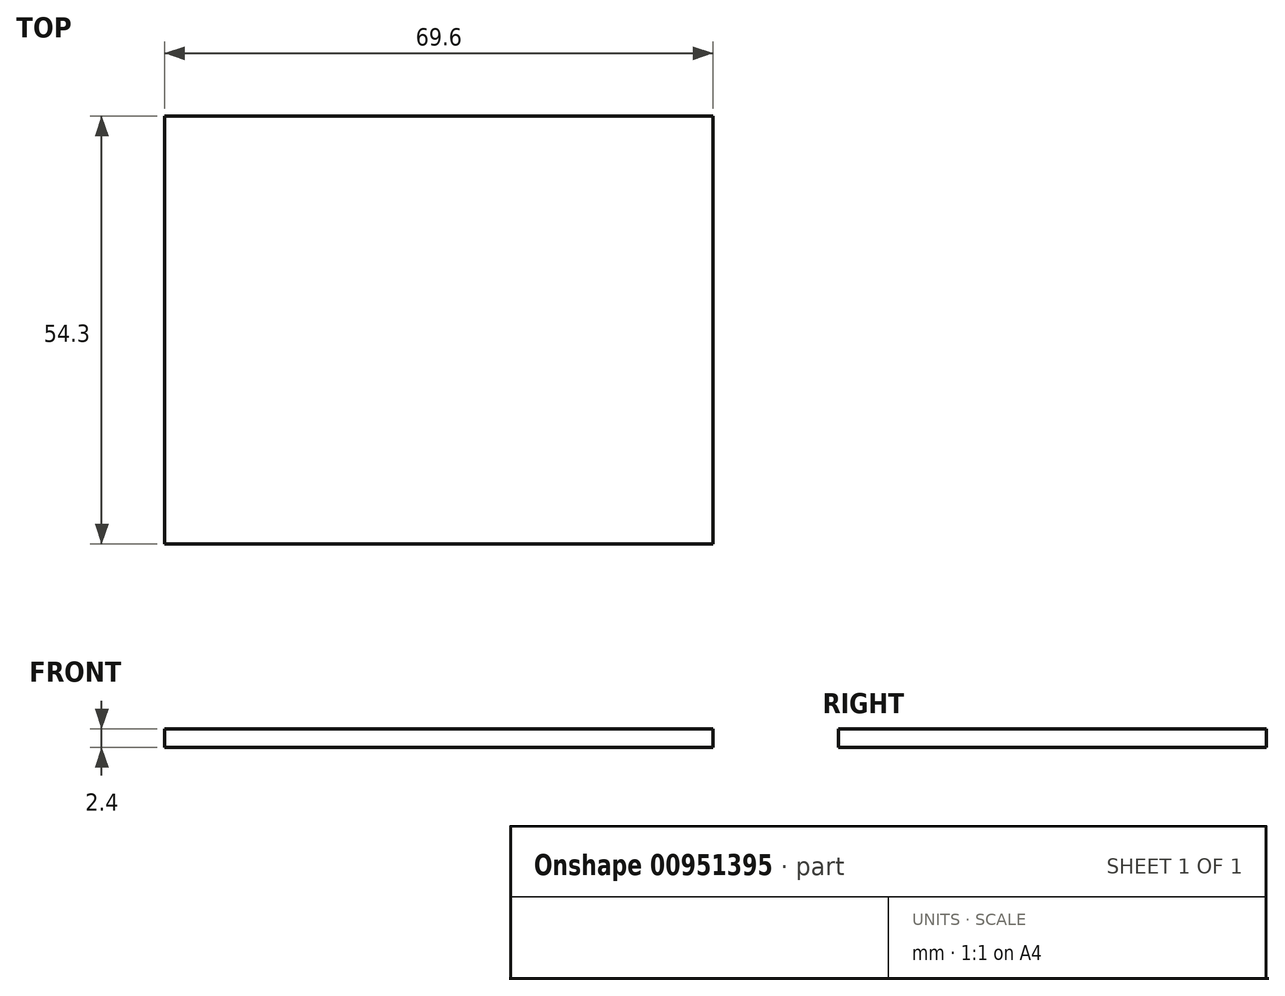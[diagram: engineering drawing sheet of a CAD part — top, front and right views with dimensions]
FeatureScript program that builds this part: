
annotation { "Feature Type Name" : "Feature", "Feature Type Description" : "" }
export const myFeature = defineFeature(function(context is Context, id is Id, definition is map)
    precondition{}
    {
        {
            var Q0;
            Q0=qCreatedBy(makeId("Top.planeOp"),FACE);
            var sketch = newSketch(context, id + "F0", { "sketchPlane" : qUnion([Q0])});
            skLineSegment(sketch, "E0", {"start": v(-69.6, 54.3) * mm, "end": v(-69.6, 0) * mm});
            skLineSegment(sketch, "E1", {"start": v(-69.6, 0) * mm, "end": v(0, 0) * mm});
            skLineSegment(sketch, "E2", {"start": v(0, 0) * mm, "end": v(0, 54.3) * mm});
            skLineSegment(sketch, "E3", {"start": v(0, 54.3) * mm, "end": v(-69.6, 54.3) * mm});
            skSolve(sketch);
        }
        {
            var Q0;
            Q0 = qSketchRegion(id + "F0", true);
            extrude(context, id + "F1", {"entities" : qUnion([Q0]), "depth" : 2.4 * mm, "offsetDistance" : 25 * mm});
        }
    });
